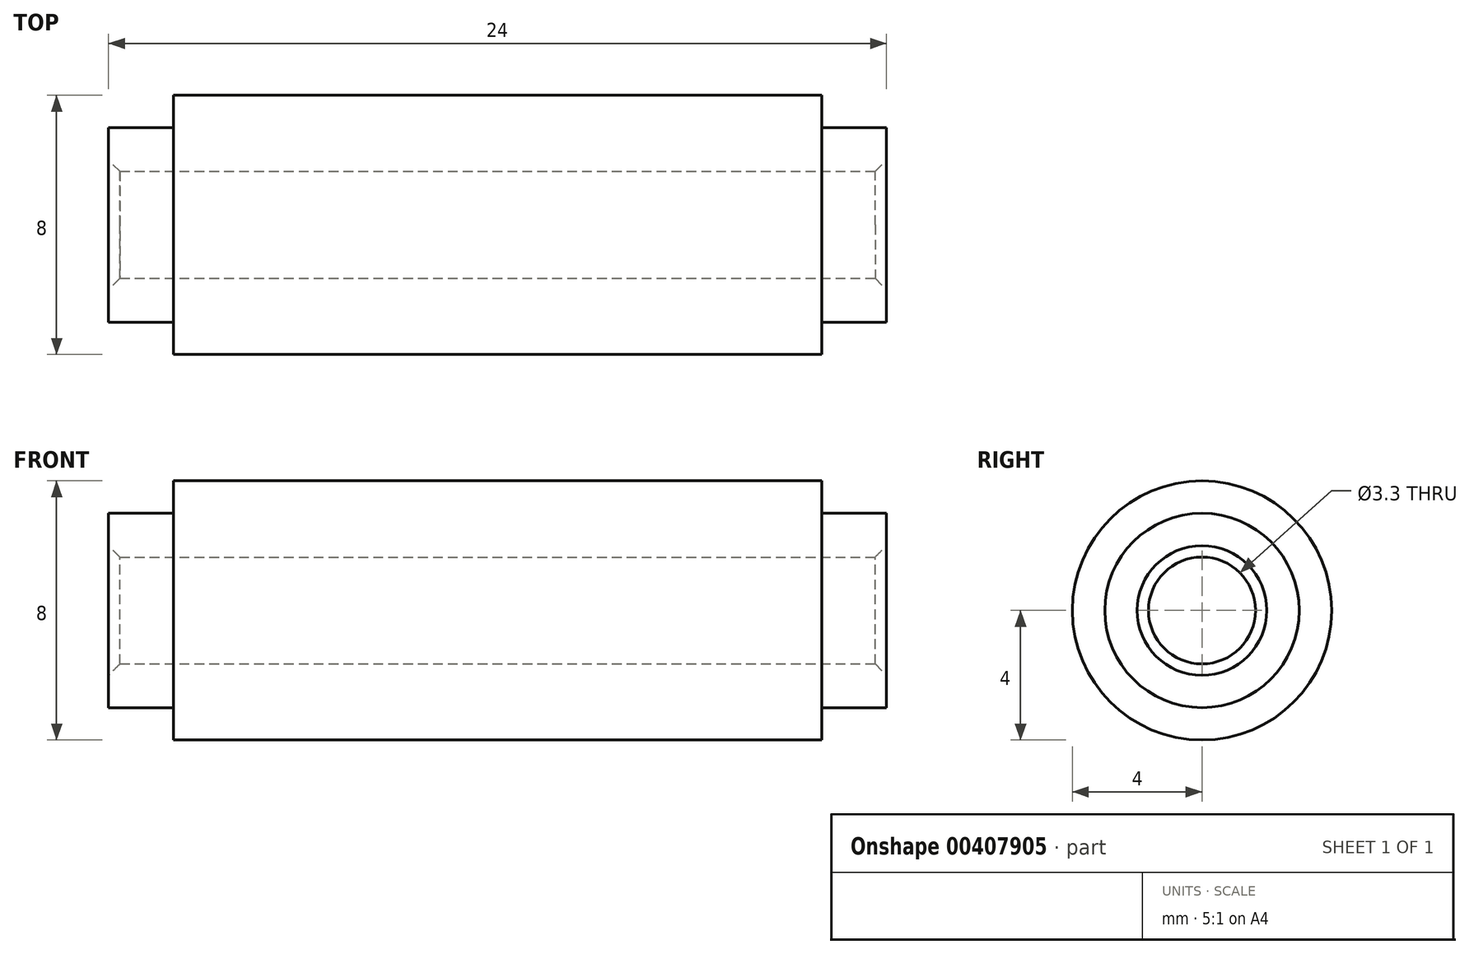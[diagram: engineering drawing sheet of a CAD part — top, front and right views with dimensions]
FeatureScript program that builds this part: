
annotation { "Feature Type Name" : "Feature", "Feature Type Description" : "" }
export const myFeature = defineFeature(function(context is Context, id is Id, definition is map)
    precondition{}
    {
        {
            var Q0;
            Q0=qCreatedBy(makeId("Front.planeOp"),FACE);
            var sketch = newSketch(context, id + "F0", { "sketchPlane" : qUnion([Q0])});
            skLineSegment(sketch, "E0", {"start": v(0, 3) * mm, "end": v(-2, 3) * mm});
            skLineSegment(sketch, "E1", {"start": v(-2, 3) * mm, "end": v(-2, 4) * mm});
            skLineSegment(sketch, "E2", {"start": v(-2, 4) * mm, "end": v(-22, 4) * mm});
            skLineSegment(sketch, "E3", {"start": v(-22, 4) * mm, "end": v(-22, 3) * mm});
            skLineSegment(sketch, "E4", {"start": v(-22, 3) * mm, "end": v(-24, 3) * mm});
            skLineSegment(sketch, "E5", {"start": v(0, 3) * mm, "end": v(0, 1.65) * mm});
            skLineSegment(sketch, "E6", {"start": v(0, 1.65) * mm, "end": v(-24, 1.65) * mm});
            skLineSegment(sketch, "E7", {"start": v(-24, 1.65) * mm, "end": v(-24, 3) * mm});
            skLineSegment(sketch, "E8", {"start": v(0, 0) * mm, "end": v(-24, 0) * mm, "construction": true});
            skSolve(sketch);
        }
        {
            var Q0;
            Q0 = qSketchRegion(id + "F0", true);
            var Q1;
            Q1=makeQuery(id+"F0.imprint","IMPRINT",FACE,{"disambiguationData":[TD([[makeQuery(id+"F0.imprint","IMPRINT",EDGE,{"derivedFrom":sQuery(id+"F0.wireOp",EDGE,"E0")}),1.0]])]});
            var Q2;
            Q2=sQuery(id+"F0.wireOp",EDGE,"E8");
            revolve(context, id + "F1", {"entities" : qUnion([Q0, Q1]), "axis" : qUnion([Q2]), "revolveType" : RevolveType.FULL});
        }
        {
            var Q0;
            Q0=makeQuery(id+"F1.opRevolve","SWEPT_EDGE",EDGE,{"disambiguationData":[OSD([sQuery(id+"F0.wireOp",EDGE,"E6"),sQuery(id+"F0.wireOp",EDGE,"E7")])]});
            var Q1;
            Q1=makeQuery(id+"F1.opRevolve","SWEPT_EDGE",EDGE,{"disambiguationData":[OSD([sQuery(id+"F0.wireOp",EDGE,"E5"),sQuery(id+"F0.wireOp",EDGE,"E6")])]});
            chamfer(context, id + "F2", {"entities" : qUnion([Q0, Q1]), "width" : .35 * mm, "tangentPropagation" : true});
        }
    });
